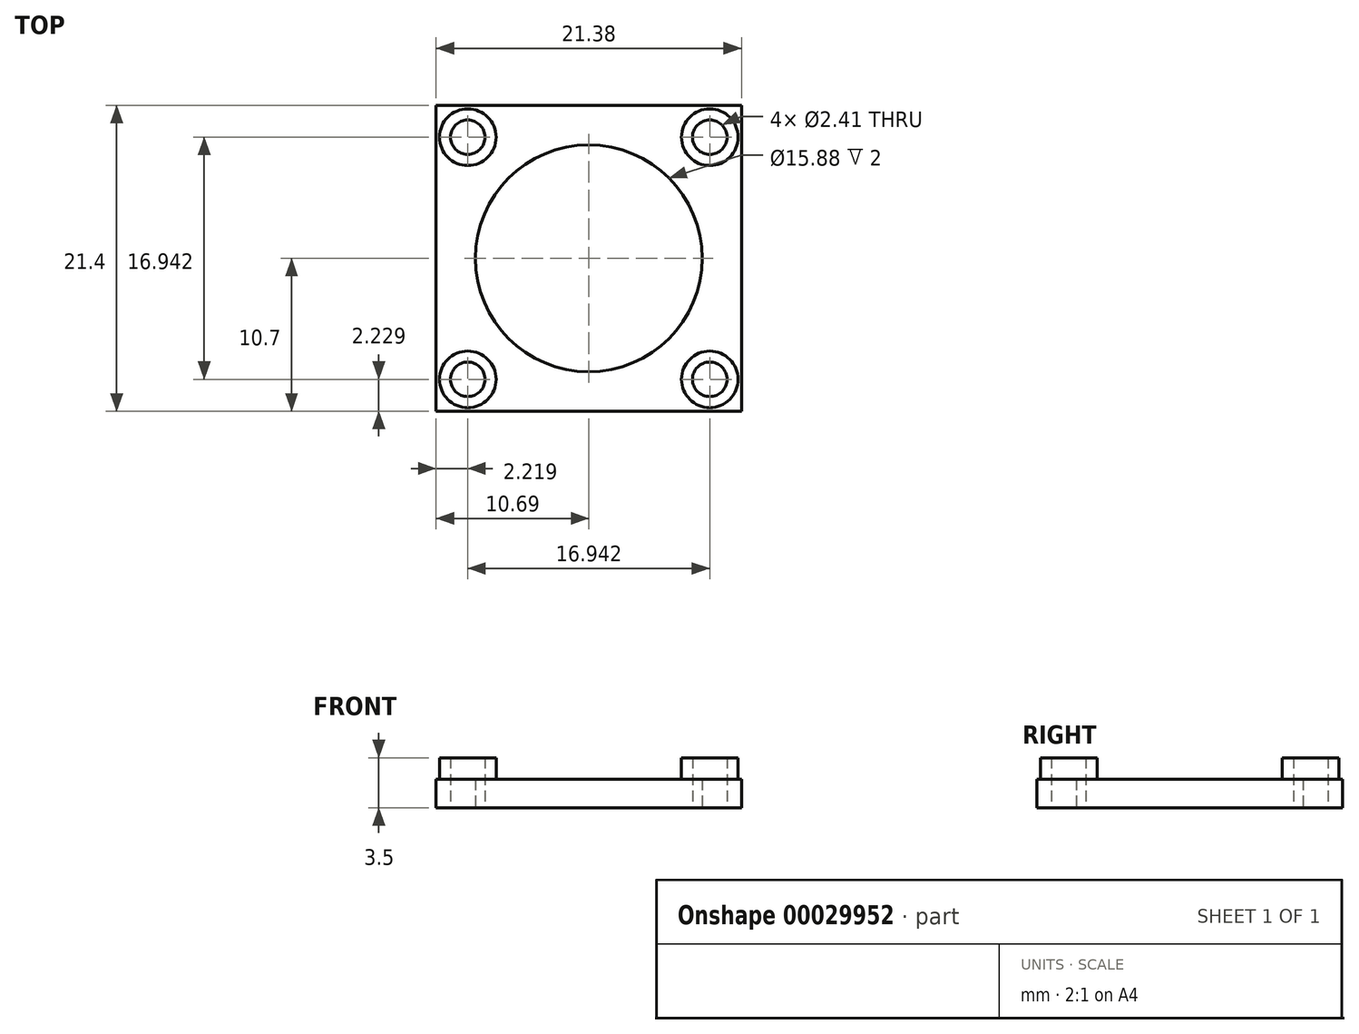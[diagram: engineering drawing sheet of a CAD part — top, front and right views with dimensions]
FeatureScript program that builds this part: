
annotation { "Feature Type Name" : "Feature", "Feature Type Description" : "" }
export const myFeature = defineFeature(function(context is Context, id is Id, definition is map)
    precondition{}
    {
        {
            var Q0;
            Q0=qCreatedBy(makeId("Top.planeOp"),FACE);
            var sketch = newSketch(context, id + "F0", { "sketchPlane" : qUnion([Q0])});
            skLineSegment(sketch, "E0.rect.bottom", {"start": v(10.7, 10.7) * mm, "end": v(-10.7, 10.7) * mm});
            skLineSegment(sketch, "E0.rect.top", {"start": v(10.7, -10.7) * mm, "end": v(-10.7, -10.7) * mm});
            skLineSegment(sketch, "E0.rect.left", {"start": v(10.7, 10.7) * mm, "end": v(10.7, -10.7) * mm});
            skLineSegment(sketch, "E0.rect.right", {"start": v(-10.7, 10.7) * mm, "end": v(-10.7, -10.7) * mm});
            skPoint(sketch, "E0.rect.middle", {"position": v(0, 0) * mm});
            skCircle(sketch, "E1", {"center": v(0, 0) * mm, "radius": 7.94 * mm});
            skLineSegment(sketch, "E2.rect.bottom", {"start": v(-8.47, 8.47) * mm, "end": v(8.47, 8.47) * mm, "construction": true});
            skLineSegment(sketch, "E2.rect.top", {"start": v(-8.47, -8.47) * mm, "end": v(8.47, -8.47) * mm, "construction": true});
            skLineSegment(sketch, "E2.rect.left", {"start": v(-8.47, 8.47) * mm, "end": v(-8.47, -8.47) * mm, "construction": true});
            skLineSegment(sketch, "E2.rect.right", {"start": v(8.47, 8.47) * mm, "end": v(8.47, -8.47) * mm, "construction": true});
            skCircle(sketch, "E3", {"center": v(-8.47, 8.47) * mm, "radius": 1.98 * mm});
            skCircle(sketch, "E4", {"center": v(-8.47, 8.47) * mm, "radius": 1.2 * mm});
            skCircle(sketch, "E5.0.1.0", {"center": v(-8.47, -8.47) * mm, "radius": 1.98 * mm});
            skCircle(sketch, "E5.0.1.1", {"center": v(-8.47, -8.47) * mm, "radius": 1.2 * mm});
            skCircle(sketch, "E5.1.0.0", {"center": v(8.47, 8.47) * mm, "radius": 1.98 * mm});
            skCircle(sketch, "E5.1.0.1", {"center": v(8.47, 8.47) * mm, "radius": 1.2 * mm});
            skCircle(sketch, "E5.1.1.0", {"center": v(8.47, -8.47) * mm, "radius": 1.98 * mm});
            skCircle(sketch, "E5.1.1.1", {"center": v(8.47, -8.47) * mm, "radius": 1.2 * mm});
            skSolve(sketch);
        }
        {
            var Q0;
            Q0=makeQuery(id+"F0.imprint","IMPRINT",FACE,{"disambiguationData":[TD([[makeQuery(id+"F0.imprint","IMPRINT",EDGE,{"derivedFrom":sQuery(id+"F0.wireOp",EDGE,"E0.rect.bottom")}),1.0]])]});
            var Q1;
            Q1=makeQuery(id+"F0.imprint","IMPRINT",FACE,{"disambiguationData":[TD([[makeQuery(id+"F0.imprint","IMPRINT",EDGE,{"derivedFrom":sQuery(id+"F0.wireOp",EDGE,"E5.0.1.0")}),1.0]])]});
            var Q2;
            Q2=makeQuery(id+"F0.imprint","IMPRINT",FACE,{"disambiguationData":[TD([[makeQuery(id+"F0.imprint","IMPRINT",EDGE,{"derivedFrom":sQuery(id+"F0.wireOp",EDGE,"E5.1.1.0")}),1.0]])]});
            var Q3;
            Q3=makeQuery(id+"F0.imprint","IMPRINT",FACE,{"disambiguationData":[TD([[makeQuery(id+"F0.imprint","IMPRINT",EDGE,{"derivedFrom":sQuery(id+"F0.wireOp",EDGE,"E5.1.0.0")}),1.0]])]});
            var Q4;
            Q4=makeQuery(id+"F0.imprint","IMPRINT",FACE,{"disambiguationData":[TD([[makeQuery(id+"F0.imprint","IMPRINT",EDGE,{"derivedFrom":sQuery(id+"F0.wireOp",EDGE,"E3")}),1.0]])]});
            extrude(context, id + "F1", {"entities" : qUnion([Q0, Q1, Q2, Q3, Q4]), "depth" : 2 * mm});
        }
        {
            var Q0;
            Q0=makeQuery(id+"F0.imprint","IMPRINT",FACE,{"disambiguationData":[TD([[makeQuery(id+"F0.imprint","IMPRINT",EDGE,{"derivedFrom":sQuery(id+"F0.wireOp",EDGE,"E5.0.1.0")}),1.0]])]});
            var Q1;
            Q1=makeQuery(id+"F0.imprint","IMPRINT",FACE,{"disambiguationData":[TD([[makeQuery(id+"F0.imprint","IMPRINT",EDGE,{"derivedFrom":sQuery(id+"F0.wireOp",EDGE,"E5.1.1.0")}),1.0]])]});
            var Q2;
            Q2=makeQuery(id+"F0.imprint","IMPRINT",FACE,{"disambiguationData":[TD([[makeQuery(id+"F0.imprint","IMPRINT",EDGE,{"derivedFrom":sQuery(id+"F0.wireOp",EDGE,"E5.1.0.0")}),1.0]])]});
            var Q3;
            Q3=makeQuery(id+"F0.imprint","IMPRINT",FACE,{"disambiguationData":[TD([[makeQuery(id+"F0.imprint","IMPRINT",EDGE,{"derivedFrom":sQuery(id+"F0.wireOp",EDGE,"E3")}),1.0]])]});
            extrude(context, id + "F2", {"entities" : qUnion([Q0, Q1, Q2, Q3]), "operationType" : NewBodyOperationType.ADD, "depth" : 3.5 * mm});
        }
    });
